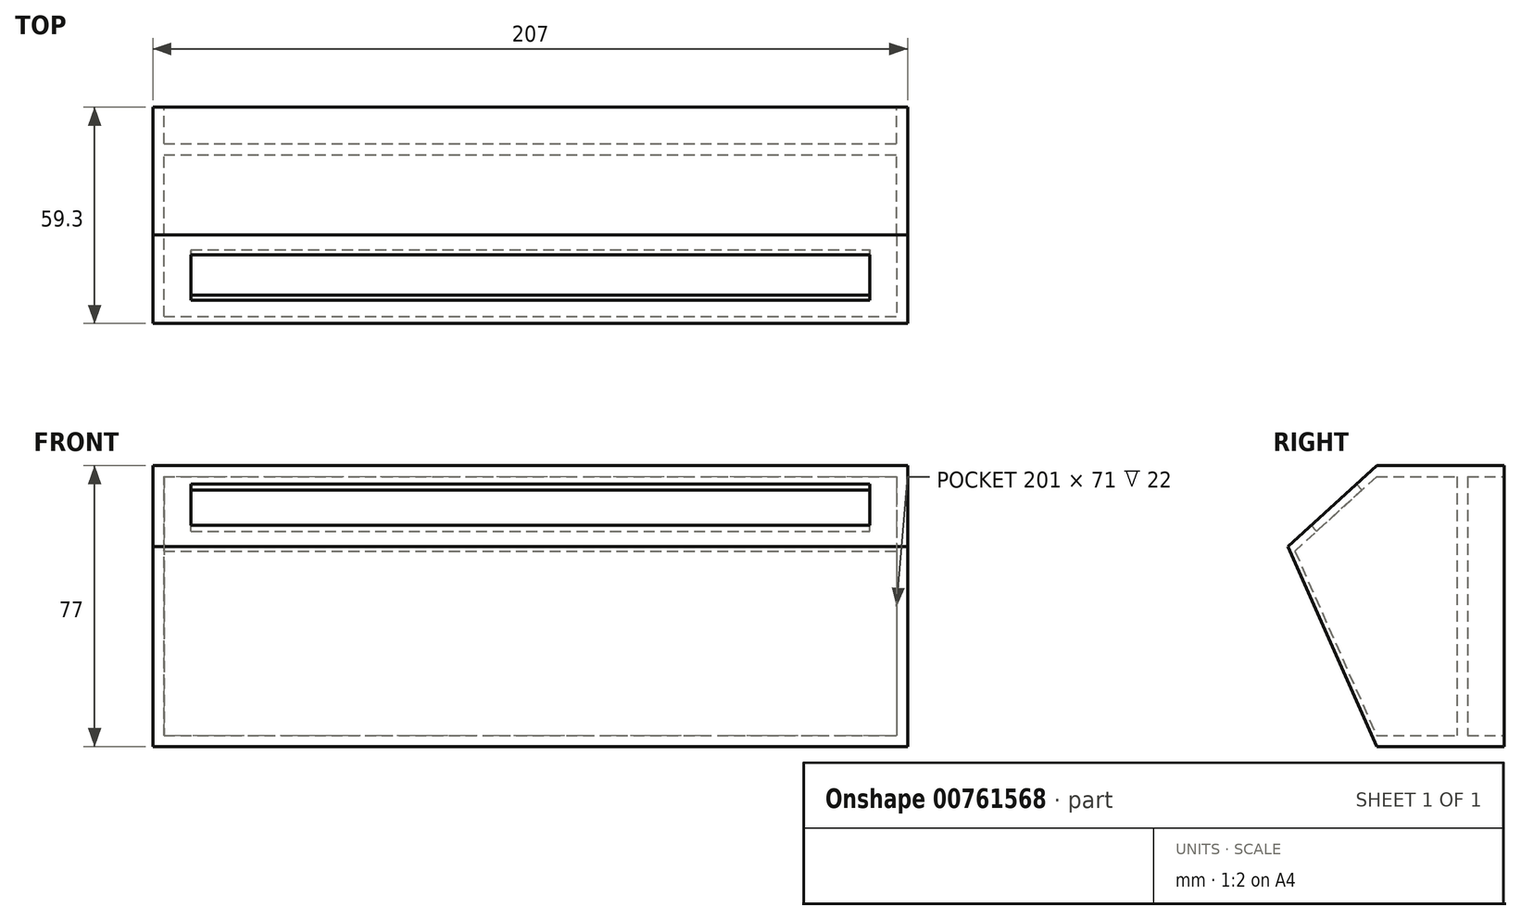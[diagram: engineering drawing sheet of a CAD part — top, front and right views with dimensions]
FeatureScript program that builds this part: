
annotation { "Feature Type Name" : "Feature", "Feature Type Description" : "" }
export const myFeature = defineFeature(function(context is Context, id is Id, definition is map)
    precondition{}
    {
        {
            var Q0;
            Q0=qCreatedBy(makeId("Front.planeOp"),FACE);
            var sketch = newSketch(context, id + "F0", { "sketchPlane" : qUnion([Q0])});
            skLineSegment(sketch, "E0.bottom", {"start": v(-103.5, 38.5) * mm, "end": v(103.5, 38.5) * mm});
            skLineSegment(sketch, "E0.top", {"start": v(-103.5, -38.5) * mm, "end": v(103.5, -38.5) * mm});
            skLineSegment(sketch, "E0.left", {"start": v(-103.5, 38.5) * mm, "end": v(-103.5, -38.5) * mm});
            skLineSegment(sketch, "E0.right", {"start": v(103.5, 38.5) * mm, "end": v(103.5, -38.5) * mm});
            skPoint(sketch, "E0.middle", {"position": v(0, 0) * mm});
            skLineSegment(sketch, "E1.0", {"start": v(-100.5, 35.5) * mm, "end": v(100.5, 35.5) * mm});
            skLineSegment(sketch, "E1.1", {"start": v(-100.5, 35.5) * mm, "end": v(-100.5, -35.5) * mm});
            skLineSegment(sketch, "E1.2", {"start": v(-100.5, -35.5) * mm, "end": v(100.5, -35.5) * mm});
            skLineSegment(sketch, "E1.3", {"start": v(100.5, 35.5) * mm, "end": v(100.5, -35.5) * mm});
            skSolve(sketch);
        }
        {
            var Q0;
            Q0=makeQuery(id+"F0.imprint","IMPRINT",FACE,{"disambiguationData":[TD([[makeQuery(id+"F0.imprint","IMPRINT",EDGE,{"derivedFrom":sQuery(id+"F0.wireOp",EDGE,"E1.0")}),-1.0]])]});
            extrude(context, id + "F1", {"entities" : qUnion([Q0]), "depth" : 3 * mm, "offsetDistance" : 25 * mm});
        }
        {
            var Q0;
            Q0=makeQuery(id+"F0.imprint","IMPRINT",FACE,{"disambiguationData":[TD([[makeQuery(id+"F0.imprint","IMPRINT",EDGE,{"derivedFrom":sQuery(id+"F0.wireOp",EDGE,"E0.bottom")}),-1.0]])]});
            extrude(context, id + "F2", {"entities" : qUnion([Q0]), "operationType" : NewBodyOperationType.ADD, "depth" : 25 * mm, "offsetDistance" : 25 * mm, "hasSecondDirection" : true, "secondDirectionOppositeDirection" : true, "secondDirectionDepth" : 10 * mm});
        }
        {
            var Q0;
            Q0=makeQuery(id+"F2.opExtrude","SWEPT_FACE",FACE,{"disambiguationData":[OSD([sQuery(id+"F0.wireOp",EDGE,"E0.right")])]});
            var sketch = newSketch(context, id + "F3", { "sketchPlane" : qUnion([Q0])});
            skLineSegment(sketch, "E2", {"start": v(-25, -38.5) * mm, "end": v(-49.3, 16.36) * mm});
            skLineSegment(sketch, "E3", {"start": v(-47.4, 15.09) * mm, "end": v(-25, -35.5) * mm});
            skPoint(sketch, "E4.0", {"position": v(-25, 35.5) * mm});
            skPoint(sketch, "E5.0", {"position": v(-25, -35.5) * mm});
            skLineSegment(sketch, "E6", {"start": v(-25, 35.5) * mm, "end": v(-47.4, 15.09) * mm});
            skLineSegment(sketch, "E7", {"start": v(-49.3, 16.36) * mm, "end": v(-25, 38.5) * mm});
            skSolve(sketch);
        }
        {
            var Q0;
            {var subQ0=sQuery(id+"F3.wireOp",EDGE,"E3");Q0=makeQuery(id+"F3.imprint","IMPRINT",FACE,{"disambiguationData":[TD([[makeQuery(id+"F3.imprint","IMPRINT",EDGE,{"derivedFrom":subQ0}),1.0]])]});}
            var Q1;
            {var subQ3=sQuery(id+"F3.wireOp",EDGE,"E2");Q1=makeQuery(id+"F3.imprint","IMPRINT",FACE,{"disambiguationData":[TD([[makeQuery(id+"F3.imprint","IMPRINT",EDGE,{"derivedFrom":subQ3}),-1.0]])]});}
            var Q2;
            {var subQ0=sQuery(id+"F0.wireOp",EDGE,"E1.3");var subQ1=sQuery(id+"F0.wireOp",EDGE,"E1.2");var subQ2=sQuery(id+"F0.wireOp",EDGE,"E1.1");var subQ3=sQuery(id+"F0.wireOp",EDGE,"E1.0");Q2=makeQuery(id+"F2.boolean.opBoolean","SPLIT",FACE,{"disambiguationData":[TD([makeQuery(id+"F1.opExtrude","CAP_FACE",FACE,{"disambiguationData":[OSD([subQ3,subQ2,subQ1,subQ0])],"isStart":false})])],"derivedFrom":makeQuery(id+"F2.opExtrude","SWEPT_FACE",FACE,{"disambiguationData":[OSD([subQ0])]})});}
            extrude(context, id + "F4", {"entities" : qUnion([Q0, Q1]), "operationType" : NewBodyOperationType.ADD, "endBound" : BoundingType.UP_TO_SURFACE, "oppositeDirection" : true, "depth" : 25 * mm, "endBoundEntityFace" : qUnion([Q2]), "offsetDistance" : 25 * mm});
        }
        {
            var Q0;
            {var subQ3=sQuery(id+"F3.wireOp",EDGE,"E2");Q0=makeQuery(id+"F3.imprint","IMPRINT",FACE,{"disambiguationData":[TD([[makeQuery(id+"F3.imprint","IMPRINT",EDGE,{"derivedFrom":subQ3}),-1.0]])]});}
            var Q1;
            Q1=makeQuery(id+"F2.opExtrude","SWEPT_FACE",FACE,{"disambiguationData":[OSD([sQuery(id+"F0.wireOp",EDGE,"E0.left")])]});
            extrude(context, id + "F5", {"entities" : qUnion([Q0]), "operationType" : NewBodyOperationType.ADD, "endBound" : BoundingType.UP_TO_SURFACE, "oppositeDirection" : true, "depth" : 25 * mm, "endBoundEntityFace" : qUnion([Q1]), "offsetDistance" : 25 * mm});
        }
        {
            var Q0;
            {var subQ0=sQuery(id+"F0.wireOp",EDGE,"E0.left");Q0=makeQuery(id+"F5.boolean.opBoolean","MERGE",FACE,{"derivedFrom":[makeQuery(id+"F2.opExtrude","SWEPT_FACE",FACE,{"disambiguationData":[OSD([subQ0])]}),makeQuery(id+"F5.opExtrude","CAP_FACE",FACE,{"disambiguationData":[OSD([subQ0])],"isStart":false})]});}
            var sketch = newSketch(context, id + "F6", { "sketchPlane" : qUnion([Q0])});
            skLineSegment(sketch, "E8", {"start": v(25, -35.5) * mm, "end": v(25, 35.5) * mm});
            skLineSegment(sketch, "E9", {"start": v(25, 35.5) * mm, "end": v(47.4, 15.09) * mm});
            skLineSegment(sketch, "E10", {"start": v(47.4, 15.09) * mm, "end": v(25, -35.5) * mm});
            skSolve(sketch);
        }
        {
            var Q0;
            Q0=makeQuery(id+"F6.imprint","IMPRINT",FACE,{"disambiguationData":[TD([[makeQuery(id+"F6.imprint","IMPRINT",EDGE,{"derivedFrom":sQuery(id+"F6.wireOp",EDGE,"E8")}),1.0]])]});
            var Q1;
            {var subQ0=sQuery(id+"F0.wireOp",EDGE,"E1.3");var subQ1=sQuery(id+"F0.wireOp",EDGE,"E1.2");var subQ2=sQuery(id+"F0.wireOp",EDGE,"E1.1");var subQ3=sQuery(id+"F0.wireOp",EDGE,"E1.0");Q1=makeQuery(id+"F2.boolean.opBoolean","SPLIT",FACE,{"disambiguationData":[TD([makeQuery(id+"F1.opExtrude","CAP_FACE",FACE,{"disambiguationData":[OSD([subQ3,subQ2,subQ1,subQ0])],"isStart":false})])],"derivedFrom":makeQuery(id+"F2.opExtrude","SWEPT_FACE",FACE,{"disambiguationData":[OSD([subQ2])]})});}
            extrude(context, id + "F7", {"entities" : qUnion([Q0]), "operationType" : NewBodyOperationType.ADD, "endBound" : BoundingType.UP_TO_SURFACE, "oppositeDirection" : true, "depth" : 25 * mm, "endBoundEntityFace" : qUnion([Q1]), "offsetDistance" : 25 * mm});
        }
        {
            var Q0;
            {var subQ0=sQuery(id+"F3.wireOp",EDGE,"E7");Q0=makeQuery(id+"F5.boolean.opBoolean","MERGE",FACE,{"derivedFrom":[makeQuery(id+"F4.opExtrude","SWEPT_FACE",FACE,{"disambiguationData":[OSD([subQ0])]}),makeQuery(id+"F5.opExtrude","SWEPT_FACE",FACE,{"disambiguationData":[OSD([subQ0])]})]});}
            var sketch = newSketch(context, id + "F8", { "sketchPlane" : qUnion([Q0])});
            skLineSegment(sketch, "E11.bottom", {"start": v(93.08, 0) * mm, "end": v(-93.08, 0) * mm});
            skLineSegment(sketch, "E11.top", {"start": v(93.08, -16.86) * mm, "end": v(-93.08, -16.86) * mm});
            skLineSegment(sketch, "E11.left", {"start": v(93.08, 0) * mm, "end": v(93.08, -16.86) * mm});
            skLineSegment(sketch, "E11.right", {"start": v(-93.08, 0) * mm, "end": v(-93.08, -16.86) * mm});
            skPoint(sketch, "E11.middle", {"position": v(0, -8.43) * mm});
            skSolve(sketch);
        }
        {
            var Q0;
            Q0=makeQuery(id+"F8.imprint","IMPRINT",FACE,{"disambiguationData":[TD([[makeQuery(id+"F8.imprint","IMPRINT",EDGE,{"derivedFrom":sQuery(id+"F8.wireOp",EDGE,"E11.bottom")}),1.0]])]});
            extrude(context, id + "F9", {"entities" : qUnion([Q0]), "operationType" : NewBodyOperationType.REMOVE, "endBound" : BoundingType.UP_TO_NEXT, "oppositeDirection" : true, "depth" : 25 * mm, "offsetDistance" : 25 * mm});
        }
    });
